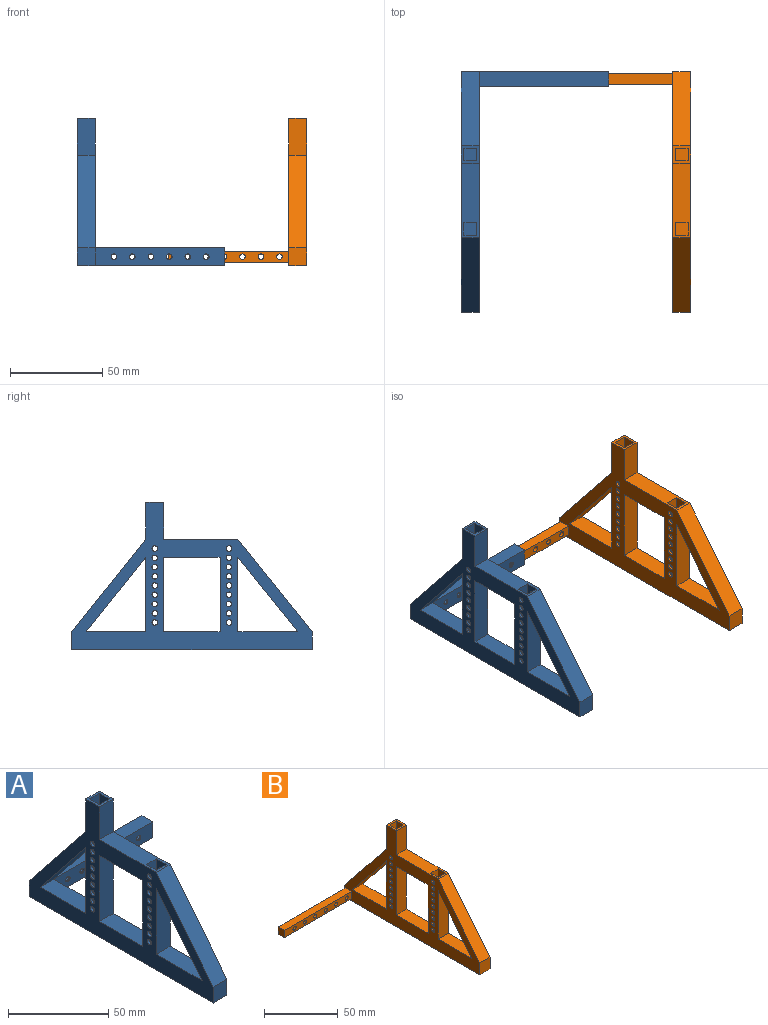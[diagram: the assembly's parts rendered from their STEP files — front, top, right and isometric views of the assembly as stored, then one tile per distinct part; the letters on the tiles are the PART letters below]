
ASSEMBLY  parts=2 mates=1
PART A: 87 faces, bbox 79.7x130x79.7 mm
  f0: plane 130x79.7mm, normal (1,0,0), area 3219.9mm2, adj f1,f2,f3,f4,f5,f11,f12,f13
  f1: plane 20x9.7mm, normal (0,1,0), area 194mm2, adj f0,f6,f42,f65
  f2: plane 40.3x9.7mm, normal (0,1,0), area 390.9mm2, adj f0,f4,f6,f62
  f3: plane 40.3x9.7mm, normal (0,-1,0), area 390.9mm2, adj f0,f4,f6,f62
  f4: plane 30.45x9.7mm, normal (0,0,1), area 295.4mm2, adj f0,f2,f3,f6
  f5: plane 40.3x9.7mm, normal (0,-1,0), area 390.9mm2, adj f0,f6,f13,f35
  f6: plane 130x79.7mm, normal (-1,0,0), area 3295.2mm2, adj f1,f2,f3,f4,f5,f11,f12,f13
  f7: plane 50x7mm, normal (1,0,0), area 286.4mm2, adj f8,f10,f11,f16,f26,f27,f28,f29
  f8: plane 50x7mm, normal (0,-1,0), area 350mm2, adj f7,f9,f11,f16
  f9: plane 50x7mm, normal (-1,0,0), area 286.4mm2, adj f8,f10,f11,f16,f17,f18,f19,f20
  f10: plane 50x7mm, normal (0,1,0), area 350mm2, adj f7,f9,f11,f16
  f11: plane 40.15x9.7mm, normal (0,0,1), area 340.5mm2, adj f0,f6,f7,f8,f9,f10,f36,f37
  f12: plane 130x79.7mm, normal (0,0,-1), area 1804.2mm2, adj f0,f6,f14,f64,f71,f73
  f13: plane 32.36x9.7mm, normal (0,0,1), area 313.9mm2, adj f0,f5,f6,f35
  f14: plane 9.7x9.7mm, normal (0,-1,0), area 94.1mm2, adj f0,f6,f12,f36
  f15: plane 40.3x9.7mm, normal (0,1,0), area 390.9mm2, adj f0,f6,f63,f66
  f16: plane 7x7mm, normal (0,0,1), area 49mm2, adj f7,f8,f9,f10
  f17: cylinder r=1.5mm len=3mm, axis (1,0,0), area 12.7mm2, adj f0,f9
  f18: cylinder r=1.5mm len=3mm, axis (1,0,0), area 12.7mm2, adj f0,f9
  f19: cylinder r=1.5mm len=3mm, axis (1,0,0), area 12.7mm2, adj f0,f9
  f20: cylinder r=1.5mm len=3mm, axis (1,0,0), area 12.7mm2, adj f0,f9
  f21: cylinder r=1.5mm len=3mm, axis (1,0,0), area 12.7mm2, adj f0,f9
  f22: cylinder r=1.5mm len=3mm, axis (1,0,0), area 12.7mm2, adj f0,f9
  f23: cylinder r=1.5mm len=3mm, axis (1,0,0), area 12.7mm2, adj f0,f9
  f24: cylinder r=1.5mm len=3mm, axis (1,0,0), area 12.7mm2, adj f0,f9
  f25: cylinder r=1.5mm len=3mm, axis (1,0,0), area 12.7mm2, adj f0,f9
  f26: cylinder r=1.5mm len=3mm, axis (1,0,0), area 12.7mm2, adj f6,f7
  f27: cylinder r=1.5mm len=3mm, axis (1,0,0), area 12.7mm2, adj f6,f7
  f28: cylinder r=1.5mm len=3mm, axis (1,0,0), area 12.7mm2, adj f6,f7
  f29: cylinder r=1.5mm len=3mm, axis (1,0,0), area 12.7mm2, adj f6,f7
  f30: cylinder r=1.5mm len=3mm, axis (1,0,0), area 12.7mm2, adj f6,f7
  f31: cylinder r=1.5mm len=3mm, axis (1,0,0), area 12.7mm2, adj f6,f7
  f32: cylinder r=1.5mm len=3mm, axis (1,0,0), area 12.7mm2, adj f6,f7
  f33: cylinder r=1.5mm len=3mm, axis (1,0,0), area 12.7mm2, adj f6,f7
  f34: cylinder r=1.5mm len=3mm, axis (1,0,0), area 12.7mm2, adj f6,f7
  f35: plane 40.3x32.36mm, normal (0,0.78,-0.63), area 501.3mm2, adj f0,f5,f6,f13
  f36: plane 50x40.15mm, normal (0,-0.78,0.63), area 622mm2, adj f0,f6,f11,f14
  f37: plane 20x9.7mm, normal (0,-1,0), area 194mm2, adj f0,f6,f11,f42
  f38: plane 70x7mm, normal (0,-1,0), area 490mm2, adj f39,f41,f42,f43
  f39: plane 70x7mm, normal (-1,0,0), area 426.4mm2, adj f38,f40,f42,f43,f53,f54,f55,f56
  f40: plane 70x7mm, normal (0,1,0), area 490mm2, adj f39,f41,f42,f43
  f41: plane 70x7mm, normal (1,0,0), area 426.4mm2, adj f38,f40,f42,f43,f44,f45,f46,f47
  f42: plane 9.7x9.7mm, normal (0,0,1), area 45.1mm2, adj f0,f1,f6,f37,f38,f39,f40,f41
  f43: plane 7x7mm, normal (0,0,1), area 49mm2, adj f38,f39,f40,f41
  f44: cylinder r=1.5mm len=3mm, axis (-1,0,0), area 12.7mm2, adj f6,f41
  f45: cylinder r=1.5mm len=3mm, axis (-1,0,0), area 12.7mm2, adj f6,f41
  f46: cylinder r=1.5mm len=3mm, axis (-1,0,0), area 12.7mm2, adj f6,f41
  f47: cylinder r=1.5mm len=3mm, axis (-1,0,0), area 12.7mm2, adj f6,f41
  f48: cylinder r=1.5mm len=3mm, axis (-1,0,0), area 12.7mm2, adj f6,f41
  f49: cylinder r=1.5mm len=3mm, axis (-1,0,0), area 12.7mm2, adj f6,f41
  f50: cylinder r=1.5mm len=3mm, axis (-1,0,0), area 12.7mm2, adj f6,f41
  f51: cylinder r=1.5mm len=3mm, axis (-1,0,0), area 12.7mm2, adj f6,f41
  f52: cylinder r=1.5mm len=3mm, axis (-1,0,0), area 12.7mm2, adj f6,f41
  f53: cylinder r=1.5mm len=3mm, axis (-1,0,0), area 12.7mm2, adj f0,f39
  f54: cylinder r=1.5mm len=3mm, axis (-1,0,0), area 12.7mm2, adj f0,f39
  f55: cylinder r=1.5mm len=3mm, axis (-1,0,0), area 12.7mm2, adj f0,f39
  f56: cylinder r=1.5mm len=3mm, axis (-1,0,0), area 12.7mm2, adj f0,f39
  f57: cylinder r=1.5mm len=3mm, axis (-1,0,0), area 12.7mm2, adj f0,f39
  f58: cylinder r=1.5mm len=3mm, axis (-1,0,0), area 12.7mm2, adj f0,f39
  f59: cylinder r=1.5mm len=3mm, axis (-1,0,0), area 12.7mm2, adj f0,f39
  f60: cylinder r=1.5mm len=3mm, axis (-1,0,0), area 12.7mm2, adj f0,f39
  f61: cylinder r=1.5mm len=3mm, axis (-1,0,0), area 12.7mm2, adj f0,f39
  f62: plane 30.45x9.7mm, normal (0,0,-1), area 295.4mm2, adj f0,f2,f3,f6
  f63: plane 32.24x9.7mm, normal (0,0,1), area 312.7mm2, adj f0,f6,f15,f66
  f64: plane 79.7x9.7mm, normal (0,1,0), area 730.7mm2, adj f6,f12,f65,f70,f73,f81,f82,f83
  f65: plane 50x40mm, normal (0,0.78,0.62), area 621.1mm2, adj f0,f1,f6,f64
  f66: plane 40.3x32.24mm, normal (0,-0.78,-0.62), area 500.6mm2, adj f0,f6,f15,f63
  f67: plane 70x6mm, normal (0,0,-1), area 420mm2, adj f68,f72,f73,f74
  f68: plane 70x6mm, normal (0,-1,0), area 377.6mm2, adj f67,f69,f73,f74,f81,f82,f83,f84
  f69: plane 70x6mm, normal (0,0,1), area 420mm2, adj f68,f72,f73,f74
  f70: plane 70x7.76mm, normal (0,0,1), area 543.2mm2, adj f0,f64,f71,f73
  f71: plane 70x9.7mm, normal (0,-1,0), area 636.6mm2, adj f0,f12,f70,f73,f75,f76,f77,f78
  f72: plane 70x6mm, normal (0,1,0), area 377.6mm2, adj f67,f69,f73,f74,f75,f76,f77,f78
  f73: plane 9.7x7.76mm, normal (1,0,0), area 39.3mm2, adj f12,f64,f67,f68,f69,f70,f71,f72
  f74: plane 6x6mm, normal (1,0,0), area 36mm2, adj f67,f68,f69,f72
  f75: cylinder r=1.5mm len=3mm, axis (0,-1,0), area 8.3mm2, adj f71,f72
  f76: cylinder r=1.5mm len=3mm, axis (0,-1,0), area 8.3mm2, adj f71,f72
  f77: cylinder r=1.5mm len=3mm, axis (0,-1,0), area 8.3mm2, adj f71,f72
  f78: cylinder r=1.5mm len=3mm, axis (0,-1,0), area 8.3mm2, adj f71,f72
  f79: cylinder r=1.5mm len=3mm, axis (0,-1,0), area 8.3mm2, adj f71,f72
  f80: cylinder r=1.5mm len=3mm, axis (0,-1,0), area 8.3mm2, adj f71,f72
  f81: cylinder r=1.5mm len=3mm, axis (0,-1,0), area 8.3mm2, adj f64,f68
  f82: cylinder r=1.5mm len=3mm, axis (0,-1,0), area 8.3mm2, adj f64,f68
  f83: cylinder r=1.5mm len=3mm, axis (0,-1,0), area 8.3mm2, adj f64,f68
  f84: cylinder r=1.5mm len=3mm, axis (0,-1,0), area 8.3mm2, adj f64,f68
  f85: cylinder r=1.5mm len=3mm, axis (0,-1,0), area 8.3mm2, adj f64,f68
  f86: cylinder r=1.5mm len=3mm, axis (0,-1,0), area 8.3mm2, adj f64,f68
PART B: 78 faces, bbox 74.7x130x79.7 mm
  f0: plane 130x9.7mm, normal (0,0,-1), area 1261mm2, adj f1,f2,f8,f15
  f1: plane 9.7x9.7mm, normal (0,1,0), area 94.1mm2, adj f0,f2,f8,f65
  f2: plane 130x79.7mm, normal (1,0,0), area 3295.2mm2, adj f0,f1,f3,f4,f5,f6,f7,f13
  f3: plane 20x9.7mm, normal (0,1,0), area 194mm2, adj f2,f8,f43,f65
  f4: plane 40.3x9.7mm, normal (0,1,0), area 390.9mm2, adj f2,f6,f8,f63
  f5: plane 40.3x9.7mm, normal (0,-1,0), area 390.9mm2, adj f2,f6,f8,f63
  f6: plane 30.45x9.7mm, normal (0,0,1), area 295.4mm2, adj f2,f4,f5,f8
  f7: plane 40.3x9.7mm, normal (0,-1,0), area 390.9mm2, adj f2,f8,f14,f36
  f8: plane 130x79.7mm, normal (-1,0,0), area 3260.4mm2, adj f0,f1,f3,f4,f5,f6,f7,f13
  f9: plane 50x7mm, normal (1,0,0), area 286.4mm2, adj f10,f12,f13,f17,f27,f28,f29,f30
  f10: plane 50x7mm, normal (0,-1,0), area 350mm2, adj f9,f11,f13,f17
  f11: plane 50x7mm, normal (-1,0,0), area 286.4mm2, adj f10,f12,f13,f17,f18,f19,f20,f21
  f12: plane 50x7mm, normal (0,1,0), area 350mm2, adj f9,f11,f13,f17
  f13: plane 40.15x9.7mm, normal (0,0,1), area 340.5mm2, adj f2,f8,f9,f10,f11,f12,f37,f38
  f14: plane 32.36x9.7mm, normal (0,0,1), area 313.9mm2, adj f2,f7,f8,f36
  f15: plane 9.7x9.7mm, normal (0,-1,0), area 94.1mm2, adj f0,f2,f8,f37
  f16: plane 40.3x9.7mm, normal (0,1,0), area 390.9mm2, adj f2,f8,f64,f66
  f17: plane 7x7mm, normal (0,0,1), area 49mm2, adj f9,f10,f11,f12
  f18: cylinder r=1.5mm len=3mm, axis (1,0,0), area 12.7mm2, adj f2,f11
  f19: cylinder r=1.5mm len=3mm, axis (1,0,0), area 12.7mm2, adj f2,f11
  f20: cylinder r=1.5mm len=3mm, axis (1,0,0), area 12.7mm2, adj f2,f11
  f21: cylinder r=1.5mm len=3mm, axis (1,0,0), area 12.7mm2, adj f2,f11
  f22: cylinder r=1.5mm len=3mm, axis (1,0,0), area 12.7mm2, adj f2,f11
  f23: cylinder r=1.5mm len=3mm, axis (1,0,0), area 12.7mm2, adj f2,f11
  f24: cylinder r=1.5mm len=3mm, axis (1,0,0), area 12.7mm2, adj f2,f11
  f25: cylinder r=1.5mm len=3mm, axis (1,0,0), area 12.7mm2, adj f2,f11
  f26: cylinder r=1.5mm len=3mm, axis (1,0,0), area 12.7mm2, adj f2,f11
  f27: cylinder r=1.5mm len=3mm, axis (1,0,0), area 12.7mm2, adj f8,f9
  f28: cylinder r=1.5mm len=3mm, axis (1,0,0), area 12.7mm2, adj f8,f9
  f29: cylinder r=1.5mm len=3mm, axis (1,0,0), area 12.7mm2, adj f8,f9
  f30: cylinder r=1.5mm len=3mm, axis (1,0,0), area 12.7mm2, adj f8,f9
  f31: cylinder r=1.5mm len=3mm, axis (1,0,0), area 12.7mm2, adj f8,f9
  f32: cylinder r=1.5mm len=3mm, axis (1,0,0), area 12.7mm2, adj f8,f9
  f33: cylinder r=1.5mm len=3mm, axis (1,0,0), area 12.7mm2, adj f8,f9
  f34: cylinder r=1.5mm len=3mm, axis (1,0,0), area 12.7mm2, adj f8,f9
  f35: cylinder r=1.5mm len=3mm, axis (1,0,0), area 12.7mm2, adj f8,f9
  f36: plane 40.3x32.36mm, normal (0,0.78,-0.63), area 501.3mm2, adj f2,f7,f8,f14
  f37: plane 50x40.15mm, normal (0,-0.78,0.63), area 622mm2, adj f2,f8,f13,f15
  f38: plane 20x9.7mm, normal (0,-1,0), area 194mm2, adj f2,f8,f13,f43
  f39: plane 70x7mm, normal (0,-1,0), area 490mm2, adj f40,f42,f43,f44
  f40: plane 70x7mm, normal (-1,0,0), area 426.4mm2, adj f39,f41,f43,f44,f54,f55,f56,f57
  f41: plane 70x7mm, normal (0,1,0), area 490mm2, adj f40,f42,f43,f44
  f42: plane 70x7mm, normal (1,0,0), area 426.4mm2, adj f39,f41,f43,f44,f45,f46,f47,f48
  f43: plane 9.7x9.7mm, normal (0,0,1), area 45.1mm2, adj f2,f3,f8,f38,f39,f40,f41,f42
  f44: plane 7x7mm, normal (0,0,1), area 49mm2, adj f39,f40,f41,f42
  f45: cylinder r=1.5mm len=3mm, axis (-1,0,0), area 12.7mm2, adj f8,f42
  f46: cylinder r=1.5mm len=3mm, axis (-1,0,0), area 12.7mm2, adj f8,f42
  f47: cylinder r=1.5mm len=3mm, axis (-1,0,0), area 12.7mm2, adj f8,f42
  f48: cylinder r=1.5mm len=3mm, axis (-1,0,0), area 12.7mm2, adj f8,f42
  f49: cylinder r=1.5mm len=3mm, axis (-1,0,0), area 12.7mm2, adj f8,f42
  f50: cylinder r=1.5mm len=3mm, axis (-1,0,0), area 12.7mm2, adj f8,f42
  f51: cylinder r=1.5mm len=3mm, axis (-1,0,0), area 12.7mm2, adj f8,f42
  f52: cylinder r=1.5mm len=3mm, axis (-1,0,0), area 12.7mm2, adj f8,f42
  f53: cylinder r=1.5mm len=3mm, axis (-1,0,0), area 12.7mm2, adj f8,f42
  f54: cylinder r=1.5mm len=3mm, axis (-1,0,0), area 12.7mm2, adj f2,f40
  f55: cylinder r=1.5mm len=3mm, axis (-1,0,0), area 12.7mm2, adj f2,f40
  f56: cylinder r=1.5mm len=3mm, axis (-1,0,0), area 12.7mm2, adj f2,f40
  f57: cylinder r=1.5mm len=3mm, axis (-1,0,0), area 12.7mm2, adj f2,f40
  f58: cylinder r=1.5mm len=3mm, axis (-1,0,0), area 12.7mm2, adj f2,f40
  f59: cylinder r=1.5mm len=3mm, axis (-1,0,0), area 12.7mm2, adj f2,f40
  f60: cylinder r=1.5mm len=3mm, axis (-1,0,0), area 12.7mm2, adj f2,f40
  f61: cylinder r=1.5mm len=3mm, axis (-1,0,0), area 12.7mm2, adj f2,f40
  f62: cylinder r=1.5mm len=3mm, axis (-1,0,0), area 12.7mm2, adj f2,f40
  f63: plane 30.45x9.7mm, normal (0,0,-1), area 295.4mm2, adj f2,f4,f5,f8
  f64: plane 32.24x9.7mm, normal (0,0,1), area 312.7mm2, adj f2,f8,f16,f66
  f65: plane 50x40mm, normal (0,0.78,0.62), area 621.1mm2, adj f1,f2,f3,f8
  f66: plane 40.3x32.24mm, normal (0,-0.78,-0.62), area 500.6mm2, adj f2,f8,f16,f64
  f67: plane 65x5.9mm, normal (0,-1,0), area 341.1mm2, adj f8,f68,f70,f71,f72,f73,f74,f75
  f68: plane 65x5.9mm, normal (0,0,1), area 383.5mm2, adj f8,f67,f69,f71
  f69: plane 65x5.9mm, normal (0,1,0), area 341.1mm2, adj f8,f68,f70,f71,f72,f73,f74,f75
  f70: plane 65x5.9mm, normal (0,0,-1), area 383.5mm2, adj f8,f67,f69,f71
  f71: plane 5.9x5.9mm, normal (-1,0,0), area 34.8mm2, adj f67,f68,f69,f70
  f72: cylinder r=1.5mm len=5.9mm, axis (0,1,0), area 55.6mm2, adj f67,f69
  f73: cylinder r=1.5mm len=5.9mm, axis (0,1,0), area 55.6mm2, adj f67,f69
  f74: cylinder r=1.5mm len=5.9mm, axis (0,1,0), area 55.6mm2, adj f67,f69
  f75: cylinder r=1.5mm len=5.9mm, axis (0,1,0), area 55.6mm2, adj f67,f69
  f76: cylinder r=1.5mm len=5.9mm, axis (0,1,0), area 55.6mm2, adj f67,f69
  f77: cylinder r=1.5mm len=5.9mm, axis (0,1,0), area 55.6mm2, adj f67,f69
PLACE A t=(76.1,0,0)mm
PLACE B t=(190.38,0,0)mm
MATE slider A.f74 <-> B.f71  axis (1,0,0) through (16.1,81.12,4.85)mm
